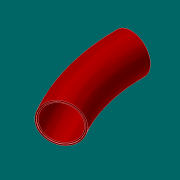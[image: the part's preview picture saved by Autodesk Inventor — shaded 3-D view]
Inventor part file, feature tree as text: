
AUTODESK INVENTOR PART (.ipt)
format: ipt  version: 2017.3 (Build 213257000, 257)  size: 233,984 bytes
history: native  units: in
note: dims shown in document units (in); Inventor stores cm internally (conversion verified against a paired STEP export)
features: extrude x4, sketch x4, revolve x2, fillet x1, chamfer x1
ambient origin geometry x8: Origin, YZ Plane, XZ Plane, XY Plane, X Axis, Y Axis, Z Axis, Center Point
bodies: Solid1 (feature_tree)
feature tree (12):
  revolve  "Revolution1"  [1 undecoded]
  extrude  "Extrusion9"  TaperAngle=30.0deg  [1 undecoded]
  sketch  "Sketch11"  dims[d34=30.5in d35=0.5in d36=0.0in]
  revolve  "Revolution3"  [1 undecoded]
  extrude  "Extrusion10"  Depth=0.0312in TaperAngle=0.0deg
  extrude  "Extrusion12"  Depth=0.0312in
  extrude  "Extrusion13"  Depth=0.0312in TaperAngle=45.0deg
  fillet  "Fillet3"  Radius=0.0034in
  chamfer  "Chamfer3"  Distance=0.25in
  sketch  "Sketch1"  dims[d0=28.5in d1=32.5in]
  sketch  "Sketch10"  dims[d2=160.0in d3=30.0deg]
  sketch  "Sketch12"  dims[d37=30.5in d39=0.25in d40=0.0in d44=0.0312in d45=0.0312in d46=0.125in d47=45.0deg d48=0.0034in d50=0.25in d51=0.0in d52=36.5in d53=0.25in d54=0.0in]
note: 3 required parameter values undecoded (feature->parameter linkage not recoverable at this tier; creation-order binding heuristic only, values carry confidence <= 0.55)